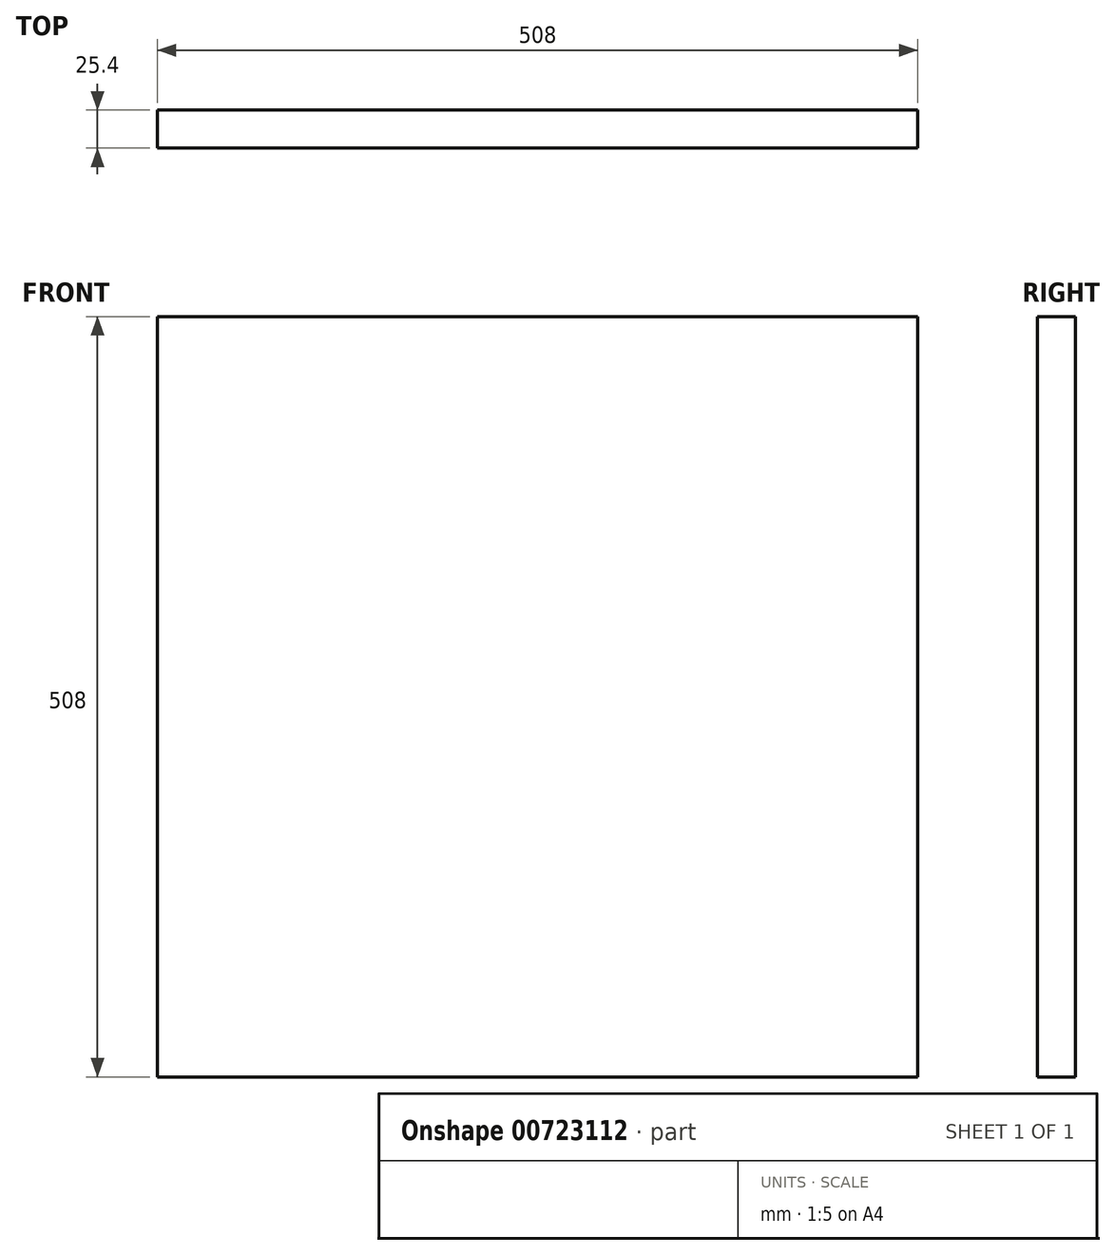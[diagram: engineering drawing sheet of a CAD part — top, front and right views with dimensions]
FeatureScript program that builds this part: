
annotation { "Feature Type Name" : "Feature", "Feature Type Description" : "" }
export const myFeature = defineFeature(function(context is Context, id is Id, definition is map)
    precondition{}
    {
        {
            var Q0;
            Q0=qCreatedBy(makeId("Front.planeOp"),FACE);
            var sketch = newSketch(context, id + "F0", { "sketchPlane" : qUnion([Q0])});
            skLineSegment(sketch, "E0.bottom", {"start": v(-578.9, 20.04) * mm, "end": v(-70.9, 20.04) * mm});
            skLineSegment(sketch, "E0.top", {"start": v(-578.9, -487.96) * mm, "end": v(-70.9, -487.96) * mm});
            skLineSegment(sketch, "E0.left", {"start": v(-578.9, 20.04) * mm, "end": v(-578.9, -487.96) * mm});
            skLineSegment(sketch, "E0.right", {"start": v(-70.9, 20.04) * mm, "end": v(-70.9, -487.96) * mm});
            skSolve(sketch);
        }
        {
            var Q0;
            Q0 = qSketchRegion(id + "F0", true);
            extrude(context, id + "F1", {"entities" : qUnion([Q0]), "depth" : 25.4 * mm, "offsetDistance" : 25.4 * mm});
        }
    });
